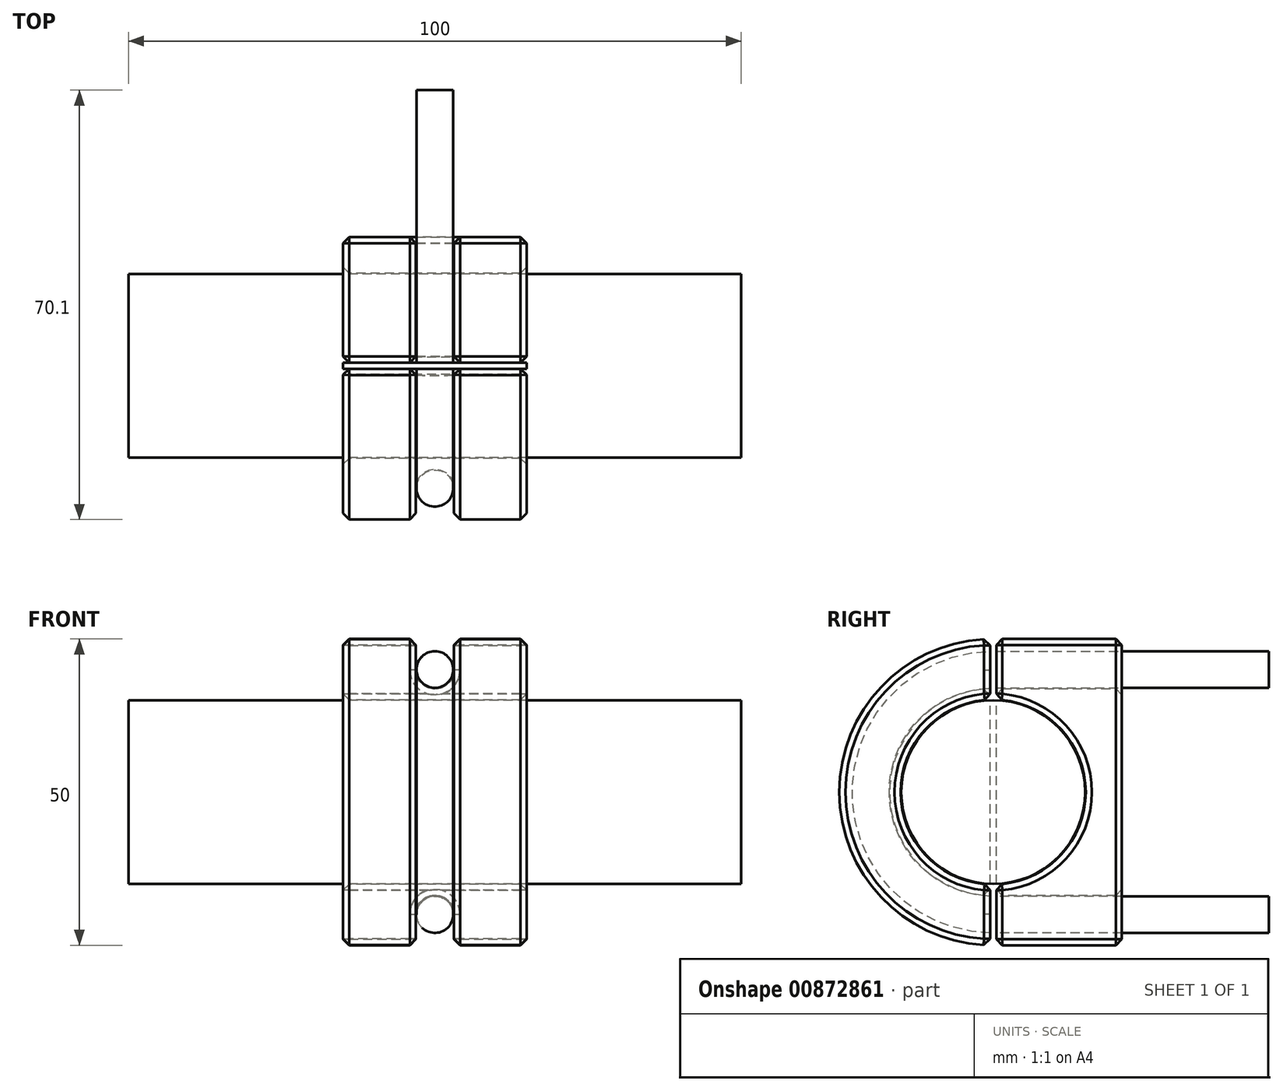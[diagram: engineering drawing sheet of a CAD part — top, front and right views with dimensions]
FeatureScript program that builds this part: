
annotation { "Feature Type Name" : "Feature", "Feature Type Description" : "" }
export const myFeature = defineFeature(function(context is Context, id is Id, definition is map)
    precondition{}
    {
        {
            assignVariable(context, id + "F0", {"name" : "Metallrohr_len", "anyValue" : 50 * mm});
        }
        {
            assignVariable(context, id + "F1", {"name" : "height", "anyValue" : 50 * mm});
        }
        {
            assignVariable(context, id + "F2", {"name" : "depth_back", "anyValue" : 21 * mm});
        }
        {
            assignVariable(context, id + "F3", {"name" : "depth_front", "anyValue" : 25.1 * mm});
        }
        {
            assignVariable(context, id + "F4", {"name" : "airgap", "anyValue" : 1 * mm});
        }
        {
            assignVariable(context, id + "F5", {"name" : "chamfer", "anyValue" : 1 * mm});
        }
        {
            var Q0;
            Q0=qCreatedBy(makeId("Right.planeOp"),FACE);
            var sketch = newSketch(context, id + "F6", { "sketchPlane" : qUnion([Q0])});
            skCircle(sketch, "E0", {"center": v(0, 0) * mm, "radius": 15 * mm});
            skLineSegment(sketch, "E1", {"start": v(0, 20) * mm, "end": v(45, 20) * mm});
            skLineSegment(sketch, "E2", {"start": v(0, -20) * mm, "end": v(45, -20) * mm});
            skArc(sketch, "E3", {"start": v(0, 20) * mm, "mid": v(-20, 0) * mm, "end": v(0, -20) * mm});
            skLineSegment(sketch, "E4", {"start": v(15, -20) * mm, "end": v(15, 20) * mm, "construction": true});
            skCircle(sketch, "E5", {"center": v(0, 0) * mm, "radius": 15.1 * mm});
            skSolve(sketch);
        }
        {
            var Q0;
            Q0=makeQuery(id+"F6.imprint","IMPRINT",FACE,{"disambiguationData":[TD([[makeQuery(id+"F6.imprint","IMPRINT",EDGE,{"derivedFrom":sQuery(id+"F6.wireOp",EDGE,"E0")}),1.0]])]});
            extrude(context, id + "F7", {"entities" : qUnion([Q0]), "depth" : getVariable(context, 'Metallrohr_len'), "offsetDistance" : 25 * mm, "hasSecondDirection" : true, "secondDirectionOppositeDirection" : true, "secondDirectionDepth" : getVariable(context, 'Metallrohr_len')});
        }
        {
            var Q0;
            Q0=qCreatedBy(makeId("Front.planeOp"),FACE);
            var sketch = newSketch(context, id + "F8", { "sketchPlane" : qUnion([Q0])});
            skCircle(sketch, "E6", {"center": v(0, 20) * mm, "radius": 3 * mm});
            skLineSegment(sketch, "E7", {"start": v(-15, 25) * mm, "end": v(15, 25) * mm});
            skLineSegment(sketch, "E8", {"start": v(15, 25) * mm, "end": v(15, -25) * mm});
            skLineSegment(sketch, "E9", {"start": v(15, -25) * mm, "end": v(-15, -25) * mm});
            skLineSegment(sketch, "E10", {"start": v(-15, -25) * mm, "end": v(-15, 25) * mm});
            skLineSegment(sketch, "E11", {"start": v(0, 0) * mm, "end": v(0, 25) * mm, "construction": true});
            skLineSegment(sketch, "E12", {"start": v(0, 0) * mm, "end": v(15, 0) * mm, "construction": true});
            skCircle(sketch, "E13", {"center": v(0, 20) * mm, "radius": 3.1 * mm});
            skLineSegment(sketch, "E14", {"start": v(3.1, 20) * mm, "end": v(3.1, 25) * mm});
            skLineSegment(sketch, "E15", {"start": v(-3.1, 20) * mm, "end": v(-3.1, 25) * mm});
            skLineSegment(sketch, "E16", {"start": v(-3.1, 25) * mm, "end": v(-3.1, 25.2) * mm});
            skLineSegment(sketch, "E17", {"start": v(-3.1, 25.2) * mm, "end": v(3.1, 25.2) * mm});
            skLineSegment(sketch, "E18", {"start": v(3.1, 25.2) * mm, "end": v(3.1, 25) * mm});
            skSolve(sketch);
        }
        {
            var Q0;
            Q0=makeQuery(id+"F8.imprint","IMPRINT",FACE,{"disambiguationData":[TD([[makeQuery(id+"F8.imprint","IMPRINT",EDGE,{"derivedFrom":sQuery(id+"F8.wireOp",EDGE,"E6")}),1.0]])]});
            var Q1;
            Q1=sQuery(id+"F6.wireOp",EDGE,"E1");
            var Q2;
            Q2=sQuery(id+"F6.wireOp",EDGE,"E3");
            var Q3;
            Q3=sQuery(id+"F6.wireOp",EDGE,"E2");
            sweep(context, id + "F9", {"profiles" : qUnion([Q0]), "path" : qUnion([Q1, Q2, Q3])});
        }
        {
            var Q0;
            Q0=makeQuery(id+"F8.imprint","IMPRINT",FACE,{"disambiguationData":[TD([[makeQuery(id+"F8.imprint","IMPRINT",EDGE,{"derivedFrom":sQuery(id+"F8.wireOp",EDGE,"E6")}),-1.0]])]});
            var Q1;
            {var subQ0=sQuery(id+"F8.wireOp",EDGE,"E14");Q1=makeQuery(id+"F8.imprint","IMPRINT",FACE,{"disambiguationData":[TD([[makeQuery(id+"F8.imprint","IMPRINT",EDGE,{"derivedFrom":subQ0}),1.0]])]});}
            var Q2;
            {var subQ2=sQuery(id+"F8.wireOp",EDGE,"E16");Q2=makeQuery(id+"F8.imprint","IMPRINT",FACE,{"disambiguationData":[TD([[makeQuery(id+"F8.imprint","IMPRINT",EDGE,{"derivedFrom":subQ2}),-1.0]])]});}
            var Q3;
            Q3=makeQuery(id+"F8.imprint","IMPRINT",FACE,{"disambiguationData":[TD([[makeQuery(id+"F8.imprint","IMPRINT",EDGE,{"derivedFrom":sQuery(id+"F8.wireOp",EDGE,"E6")}),1.0]])]});
            var Q4;
            Q4=sQuery(id+"F6.wireOp",EDGE,"E1");
            var Q5;
            Q5=sQuery(id+"F6.wireOp",EDGE,"E3");
            var Q6;
            Q6=sQuery(id+"F6.wireOp",EDGE,"E2");
            sweep(context, id + "F10", {"profiles" : qUnion([Q0, Q1, Q2, Q3]), "path" : qUnion([Q4, Q5, Q6])});
        }
        {
            var Q0;
            Q0=makeQuery(id+"F8.imprint","IMPRINT",FACE,{"disambiguationData":[TD([[makeQuery(id+"F8.imprint","IMPRINT",EDGE,{"derivedFrom":sQuery(id+"F8.wireOp",EDGE,"E7")}),-1.0]])]});
            var Q1;
            Q1=makeQuery(id+"F8.imprint","IMPRINT",FACE,{"disambiguationData":[TD([[makeQuery(id+"F8.imprint","IMPRINT",EDGE,{"derivedFrom":sQuery(id+"F8.wireOp",EDGE,"E6")}),1.0]])]});
            var Q2;
            Q2=makeQuery(id+"F8.imprint","IMPRINT",FACE,{"disambiguationData":[TD([[makeQuery(id+"F8.imprint","IMPRINT",EDGE,{"derivedFrom":sQuery(id+"F8.wireOp",EDGE,"E6")}),-1.0]])]});
            var Q3;
            {var subQ0=sQuery(id+"F8.wireOp",EDGE,"E14");Q3=makeQuery(id+"F8.imprint","IMPRINT",FACE,{"disambiguationData":[TD([[makeQuery(id+"F8.imprint","IMPRINT",EDGE,{"derivedFrom":subQ0}),1.0]])]});}
            extrude(context, id + "F11", {"entities" : qUnion([Q0, Q1, Q2, Q3]), "depth" : getVariable(context, 'depth_front'), "offsetDistance" : 25 * mm, "hasSecondDirection" : true, "secondDirectionOppositeDirection" : true, "secondDirectionDepth" : getVariable(context, 'depth_back')});
        }
        {
            var Q0;
            Q0=makeQuery(id+"F8.imprint","IMPRINT",FACE,{"disambiguationData":[TD([[makeQuery(id+"F8.imprint","IMPRINT",EDGE,{"derivedFrom":sQuery(id+"F8.wireOp",EDGE,"E6")}),1.0]])]});
            var Q1;
            Q1=makeQuery(id+"F8.imprint","IMPRINT",FACE,{"disambiguationData":[TD([[makeQuery(id+"F8.imprint","IMPRINT",EDGE,{"derivedFrom":sQuery(id+"F8.wireOp",EDGE,"E6")}),-1.0]])]});
            var Q2;
            Q2=makeQuery(id+"F8.imprint","IMPRINT",FACE,{"disambiguationData":[TD([[makeQuery(id+"F8.imprint","IMPRINT",EDGE,{"derivedFrom":sQuery(id+"F8.wireOp",EDGE,"E7")}),-1.0]])]});
            var Q3;
            {var subQ0=sQuery(id+"F8.wireOp",EDGE,"E14");Q3=makeQuery(id+"F8.imprint","IMPRINT",FACE,{"disambiguationData":[TD([[makeQuery(id+"F8.imprint","IMPRINT",EDGE,{"derivedFrom":subQ0}),1.0]])]});}
            extrude(context, id + "F12", {"entities" : qUnion([Q0, Q1, Q2, Q3]), "operationType" : NewBodyOperationType.REMOVE, "oppositeDirection" : true, "depth" : getVariable(context, 'airgap') / 2, "offsetDistance" : 25 * mm, "hasSecondDirection" : true, "secondDirectionOppositeDirection" : false, "secondDirectionDepth" : getVariable(context, 'airgap') / 2});
        }
        {
            var Q0;
            Q0=makeQuery(id+"F6.imprint","IMPRINT",FACE,{"disambiguationData":[TD([[makeQuery(id+"F6.imprint","IMPRINT",EDGE,{"derivedFrom":sQuery(id+"F6.wireOp",EDGE,"E0")}),-1.0]])]});
            var Q1;
            Q1=makeQuery(id+"F6.imprint","IMPRINT",FACE,{"disambiguationData":[TD([[makeQuery(id+"F6.imprint","IMPRINT",EDGE,{"derivedFrom":sQuery(id+"F6.wireOp",EDGE,"E0")}),1.0]])]});
            extrude(context, id + "F13", {"entities" : qUnion([Q0, Q1]), "depth" : getVariable(context, 'Metallrohr_len'), "offsetDistance" : 25 * mm, "hasSecondDirection" : true, "secondDirectionOppositeDirection" : true, "secondDirectionDepth" : getVariable(context, 'Metallrohr_len')});
        }
        {
            var Q0;
            Q0=makeQuery(id+"F11.opExtrude","CAP_EDGE",EDGE,{"disambiguationData":[OSD([sQuery(id+"F8.wireOp",EDGE,"E7")])],"isStart":false});
            var Q1;
            Q1=makeQuery(id+"F11.opExtrude","CAP_EDGE",EDGE,{"disambiguationData":[OSD([sQuery(id+"F8.wireOp",EDGE,"E9")])],"isStart":false});
            fillet(context, id + "F14", {"entities" : qUnion([Q0, Q1]), "radius" : getVariable(context, 'height') / 2, "tangentPropagation" : true, "allowEdgeOverflow" : false});
        }
        {
            var Q0;
            Q0=makeQuery(id+"F10.opSweep","SWEPT_BODY",BODY,{"disambiguationData":[OSD([sQuery(id+"F6.wireOp",EDGE,"E2"),sQuery(id+"F8.wireOp",EDGE,"E6"),sQuery(id+"F8.wireOp",EDGE,"E7"),sQuery(id+"F8.wireOp",EDGE,"E13"),sQuery(id+"F8.wireOp",EDGE,"E14"),sQuery(id+"F8.wireOp",EDGE,"E15")])]});
            var Q1;
            Q1=makeQuery(id+"F13.opExtrude","SWEPT_BODY",BODY,{"disambiguationData":[OSD([sQuery(id+"F6.wireOp",EDGE,"E5")])]});
            var Q2;
            Q2=makeQuery(id+"F12.boolean.opBoolean","SPLIT",BODY,{"disambiguationData":[OD(1.0)],"derivedFrom":makeQuery(id+"F11.opExtrude","SWEPT_BODY",BODY,{"disambiguationData":[OSD([sQuery(id+"F8.wireOp",EDGE,"E7"),sQuery(id+"F8.wireOp",EDGE,"E8"),sQuery(id+"F8.wireOp",EDGE,"E9"),sQuery(id+"F8.wireOp",EDGE,"E10")])]})});
            var Q3;
            Q3=makeQuery(id+"F12.boolean.opBoolean","SPLIT",BODY,{"disambiguationData":[OD(0.0)],"derivedFrom":makeQuery(id+"F11.opExtrude","SWEPT_BODY",BODY,{"disambiguationData":[OSD([sQuery(id+"F8.wireOp",EDGE,"E7"),sQuery(id+"F8.wireOp",EDGE,"E8"),sQuery(id+"F8.wireOp",EDGE,"E9"),sQuery(id+"F8.wireOp",EDGE,"E10")])]})});
            booleanBodies(context, id + "F15", {"operationType" : BooleanOperationType.SUBTRACTION, "tools" : qUnion([Q0, Q1]), "targets" : qUnion([Q2, Q3])});
        }
        {
            var Q0;
            {var subQ0=sQuery(id+"F8.wireOp",EDGE,"E7");var subQ1=sQuery(id+"F8.wireOp",EDGE,"E10");var subQ2=sQuery(id+"F8.wireOp",EDGE,"E9");var subQ3=sQuery(id+"F8.wireOp",EDGE,"E8");Q0=makeQuery(id+"F12.boolean.opBoolean","SPLIT",FACE,{"disambiguationData":[TD([makeQuery(id+"F11.opExtrude","CAP_FACE",FACE,{"disambiguationData":[OSD([subQ0,subQ3,subQ2,subQ1])],"isStart":false})])],"derivedFrom":makeQuery(id+"F11.opExtrude","SWEPT_FACE",FACE,{"disambiguationData":[OSD([subQ3])]})});}
            var Q1;
            {var subQ0=sQuery(id+"F8.wireOp",EDGE,"E7");var subQ1=sQuery(id+"F8.wireOp",EDGE,"E10");var subQ2=sQuery(id+"F8.wireOp",EDGE,"E9");var subQ3=sQuery(id+"F8.wireOp",EDGE,"E8");Q1=makeQuery(id+"F12.boolean.opBoolean","SPLIT",FACE,{"disambiguationData":[TD([makeQuery(id+"F11.opExtrude","CAP_FACE",FACE,{"disambiguationData":[OSD([subQ0,subQ3,subQ2,subQ1])],"isStart":false})])],"derivedFrom":makeQuery(id+"F11.opExtrude","SWEPT_FACE",FACE,{"disambiguationData":[OSD([subQ1])]})});}
            var Q2;
            {var subQ0=sQuery(id+"F8.wireOp",EDGE,"E7");var subQ1=sQuery(id+"F8.wireOp",EDGE,"E10");var subQ2=sQuery(id+"F8.wireOp",EDGE,"E9");var subQ3=sQuery(id+"F8.wireOp",EDGE,"E8");Q2=makeQuery(id+"F12.boolean.opBoolean","SPLIT",FACE,{"disambiguationData":[TD([makeQuery(id+"F11.opExtrude","CAP_FACE",FACE,{"disambiguationData":[OSD([subQ0,subQ3,subQ2,subQ1])],"isStart":true})])],"derivedFrom":makeQuery(id+"F11.opExtrude","SWEPT_FACE",FACE,{"disambiguationData":[OSD([subQ1])]})});}
            var Q3;
            {var subQ0=sQuery(id+"F8.wireOp",EDGE,"E7");var subQ1=sQuery(id+"F8.wireOp",EDGE,"E10");var subQ2=sQuery(id+"F8.wireOp",EDGE,"E9");var subQ3=sQuery(id+"F8.wireOp",EDGE,"E8");Q3=makeQuery(id+"F12.boolean.opBoolean","SPLIT",FACE,{"disambiguationData":[TD([makeQuery(id+"F11.opExtrude","CAP_FACE",FACE,{"disambiguationData":[OSD([subQ0,subQ3,subQ2,subQ1])],"isStart":true})])],"derivedFrom":makeQuery(id+"F11.opExtrude","SWEPT_FACE",FACE,{"disambiguationData":[OSD([subQ3])]})});}
            var Q4;
            {var subQ0=sQuery(id+"F8.wireOp",EDGE,"E10");var subQ1=sQuery(id+"F8.wireOp",EDGE,"E9");var subQ2=sQuery(id+"F8.wireOp",EDGE,"E8");var subQ3=sQuery(id+"F8.wireOp",EDGE,"E7");var subQ4=makeQuery(id+"F11.opExtrude","CAP_FACE",FACE,{"disambiguationData":[OSD([subQ3,subQ2,subQ1,subQ0])],"isStart":true});var subQ5=makeQuery(id+"F11.opExtrude","SWEPT_FACE",FACE,{"disambiguationData":[OSD([subQ2])]});Q4=makeQuery(id+"F15.opBoolean","SPLIT",FACE,{"disambiguationData":[TD([subQ5])],"derivedFrom":makeQuery(id+"F12.boolean.opBoolean","SPLIT",FACE,{"disambiguationData":[TD([subQ4])],"derivedFrom":makeQuery(id+"F11.opExtrude","SWEPT_FACE",FACE,{"disambiguationData":[OSD([subQ3])]})})});}
            var Q5;
            {var subQ0=sQuery(id+"F8.wireOp",EDGE,"E10");var subQ1=sQuery(id+"F8.wireOp",EDGE,"E9");var subQ2=sQuery(id+"F8.wireOp",EDGE,"E8");var subQ3=sQuery(id+"F8.wireOp",EDGE,"E7");var subQ5=makeQuery(id+"F11.opExtrude","CAP_FACE",FACE,{"disambiguationData":[OSD([subQ3,subQ2,subQ1,subQ0])],"isStart":true});var subQ6=makeQuery(id+"F11.opExtrude","SWEPT_FACE",FACE,{"disambiguationData":[OSD([subQ0])]});Q5=makeQuery(id+"F15.opBoolean","SPLIT",FACE,{"disambiguationData":[TD([subQ6])],"derivedFrom":makeQuery(id+"F12.boolean.opBoolean","SPLIT",FACE,{"disambiguationData":[TD([subQ5])],"derivedFrom":makeQuery(id+"F11.opExtrude","SWEPT_FACE",FACE,{"disambiguationData":[OSD([subQ3])]})})});}
            var Q6;
            Q6=makeQuery(id+"F11.opExtrude","CAP_FACE",FACE,{"disambiguationData":[OSD([sQuery(id+"F8.wireOp",EDGE,"E7"),sQuery(id+"F8.wireOp",EDGE,"E8"),sQuery(id+"F8.wireOp",EDGE,"E9"),sQuery(id+"F8.wireOp",EDGE,"E10")])],"isStart":true});
            var Q7;
            {var subQ0=sQuery(id+"F8.wireOp",EDGE,"E10");var subQ3=sQuery(id+"F8.wireOp",EDGE,"E7");Q7=makeQuery(id+"F15.opBoolean","SPLIT",FACE,{"disambiguationData":[TD([makeQuery(id+"F11.opExtrude","SWEPT_FACE",FACE,{"disambiguationData":[OSD([subQ0])]})])],"derivedFrom":makeQuery(id+"F14.opFillet","BLEND_FACE",FACE,{"disambiguationData":[OSD([subQ3])]})});}
            var Q8;
            {var subQ2=sQuery(id+"F8.wireOp",EDGE,"E8");var subQ3=sQuery(id+"F8.wireOp",EDGE,"E7");Q8=makeQuery(id+"F15.opBoolean","SPLIT",FACE,{"disambiguationData":[TD([makeQuery(id+"F11.opExtrude","SWEPT_FACE",FACE,{"disambiguationData":[OSD([subQ2])]})])],"derivedFrom":makeQuery(id+"F14.opFillet","BLEND_FACE",FACE,{"disambiguationData":[OSD([subQ3])]})});}
            var Q9;
            {var subQ0=sQuery(id+"F8.wireOp",EDGE,"E8");var subQ2=sQuery(id+"F8.wireOp",EDGE,"E10");var subQ3=sQuery(id+"F8.wireOp",EDGE,"E9");Q9=makeQuery(id+"F15.opBoolean","SPLIT",FACE,{"disambiguationData":[TD([makeQuery(id+"F14.opFillet","BLEND_FACE",FACE,{"disambiguationData":[OSD([subQ3])]})])],"derivedFrom":makeQuery(id+"F12.boolean.opBoolean","COPY",FACE,{"derivedFrom":makeQuery(id+"F12.opExtrude","CAP_FACE",FACE,{"disambiguationData":[OSD([sQuery(id+"F8.wireOp",EDGE,"E7"),subQ0,subQ3,subQ2])],"isStart":true})})});}
            var Q10;
            {var subQ0=sQuery(id+"F8.wireOp",EDGE,"E8");var subQ2=sQuery(id+"F8.wireOp",EDGE,"E9");var subQ3=sQuery(id+"F8.wireOp",EDGE,"E10");Q10=makeQuery(id+"F15.opBoolean","SPLIT",FACE,{"disambiguationData":[TD([makeQuery(id+"F11.opExtrude","SWEPT_FACE",FACE,{"disambiguationData":[OSD([subQ2])]})])],"derivedFrom":makeQuery(id+"F12.boolean.opBoolean","COPY",FACE,{"derivedFrom":makeQuery(id+"F12.opExtrude","CAP_FACE",FACE,{"disambiguationData":[OSD([sQuery(id+"F8.wireOp",EDGE,"E7"),subQ0,subQ2,subQ3])],"isStart":false})})});}
            var Q11;
            {var subQ0=sQuery(id+"F8.wireOp",EDGE,"E7");var subQ2=sQuery(id+"F8.wireOp",EDGE,"E8");var subQ3=sQuery(id+"F8.wireOp",EDGE,"E10");Q11=makeQuery(id+"F15.opBoolean","SPLIT",FACE,{"disambiguationData":[TD([makeQuery(id+"F11.opExtrude","SWEPT_FACE",FACE,{"disambiguationData":[OSD([subQ0])]})])],"derivedFrom":makeQuery(id+"F12.boolean.opBoolean","COPY",FACE,{"derivedFrom":makeQuery(id+"F12.opExtrude","CAP_FACE",FACE,{"disambiguationData":[OSD([subQ0,subQ2,sQuery(id+"F8.wireOp",EDGE,"E9"),subQ3])],"isStart":false})})});}
            var Q12;
            {var subQ0=sQuery(id+"F8.wireOp",EDGE,"E8");var subQ2=sQuery(id+"F8.wireOp",EDGE,"E10");var subQ3=sQuery(id+"F8.wireOp",EDGE,"E7");Q12=makeQuery(id+"F15.opBoolean","SPLIT",FACE,{"disambiguationData":[TD([makeQuery(id+"F14.opFillet","BLEND_FACE",FACE,{"disambiguationData":[OSD([subQ3])]})])],"derivedFrom":makeQuery(id+"F12.boolean.opBoolean","COPY",FACE,{"derivedFrom":makeQuery(id+"F12.opExtrude","CAP_FACE",FACE,{"disambiguationData":[OSD([subQ3,subQ0,sQuery(id+"F8.wireOp",EDGE,"E9"),subQ2])],"isStart":true})})});}
            var Q13;
            {var subQ0=sQuery(id+"F8.wireOp",EDGE,"E10");var subQ1=sQuery(id+"F8.wireOp",EDGE,"E9");var subQ2=sQuery(id+"F8.wireOp",EDGE,"E8");var subQ3=sQuery(id+"F8.wireOp",EDGE,"E7");var subQ4=makeQuery(id+"F11.opExtrude","CAP_FACE",FACE,{"disambiguationData":[OSD([subQ3,subQ2,subQ1,subQ0])],"isStart":true});var subQ5=makeQuery(id+"F11.opExtrude","SWEPT_FACE",FACE,{"disambiguationData":[OSD([subQ2])]});Q13=makeQuery(id+"F15.opBoolean","SPLIT",FACE,{"disambiguationData":[TD([subQ5])],"derivedFrom":makeQuery(id+"F12.boolean.opBoolean","SPLIT",FACE,{"disambiguationData":[TD([subQ4])],"derivedFrom":makeQuery(id+"F11.opExtrude","SWEPT_FACE",FACE,{"disambiguationData":[OSD([subQ1])]})})});}
            var Q14;
            {var subQ0=sQuery(id+"F8.wireOp",EDGE,"E10");var subQ1=sQuery(id+"F8.wireOp",EDGE,"E9");var subQ2=sQuery(id+"F8.wireOp",EDGE,"E8");var subQ3=sQuery(id+"F8.wireOp",EDGE,"E7");var subQ5=makeQuery(id+"F11.opExtrude","CAP_FACE",FACE,{"disambiguationData":[OSD([subQ3,subQ2,subQ1,subQ0])],"isStart":true});var subQ6=makeQuery(id+"F11.opExtrude","SWEPT_FACE",FACE,{"disambiguationData":[OSD([subQ0])]});Q14=makeQuery(id+"F15.opBoolean","SPLIT",FACE,{"disambiguationData":[TD([subQ6])],"derivedFrom":makeQuery(id+"F12.boolean.opBoolean","SPLIT",FACE,{"disambiguationData":[TD([subQ5])],"derivedFrom":makeQuery(id+"F11.opExtrude","SWEPT_FACE",FACE,{"disambiguationData":[OSD([subQ1])]})})});}
            chamfer(context, id + "F16", {"entities" : qUnion([Q0, Q1, Q2, Q3, Q4, Q5, Q6, Q7, Q8, Q9, Q10, Q11, Q12, Q13, Q14]), "width" : getVariable(context, 'chamfer'), "tangentPropagation" : true});
        }
    });
